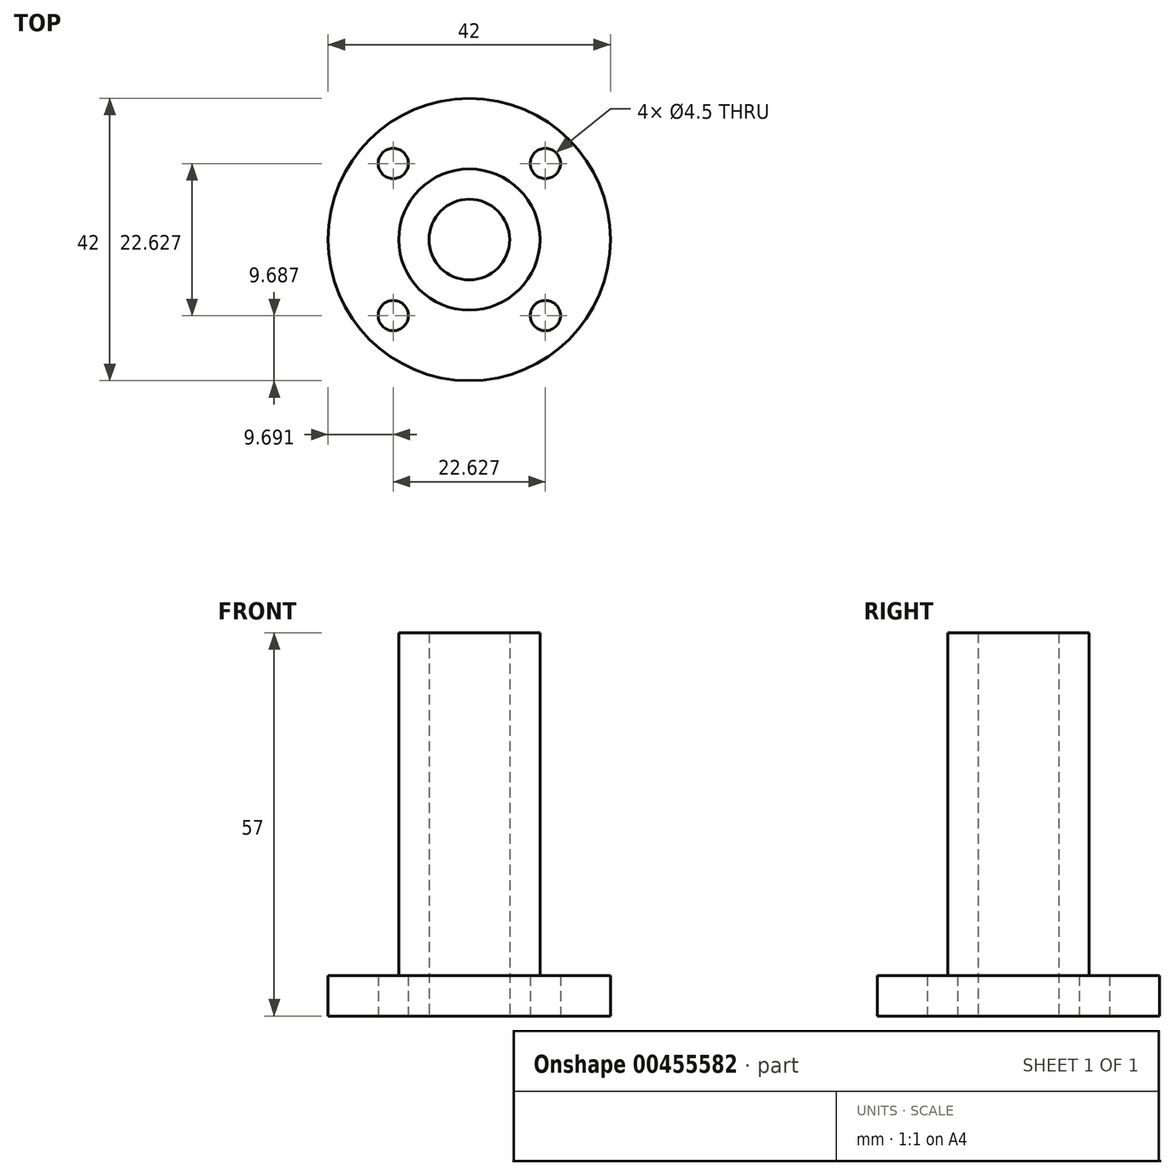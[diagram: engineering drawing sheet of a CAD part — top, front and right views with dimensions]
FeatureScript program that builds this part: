
annotation { "Feature Type Name" : "Feature", "Feature Type Description" : "" }
export const myFeature = defineFeature(function(context is Context, id is Id, definition is map)
    precondition{}
    {
        {
            var Q0;
            Q0=qCreatedBy(makeId("Top.planeOp"),FACE);
            var sketch = newSketch(context, id + "F0", { "sketchPlane" : qUnion([Q0])});
            skCircle(sketch, "E0", {"center": v(-9.89, 3.31) * mm, "radius": 6 * mm});
            skCircle(sketch, "E1", {"center": v(-9.89, 3.31) * mm, "radius": 10.5 * mm});
            skCircle(sketch, "E2", {"center": v(-9.89, 3.31) * mm, "radius": 21 * mm});
            skCircle(sketch, "E3", {"center": v(-9.89, 3.31) * mm, "radius": 16 * mm, "construction": true});
            skCircle(sketch, "E4", {"center": v(-21.2, 14.62) * mm, "radius": 2.25 * mm});
            skCircle(sketch, "E5.1.0", {"center": v(1.43, 14.62) * mm, "radius": 2.25 * mm});
            skCircle(sketch, "E5.2.0", {"center": v(1.43, -8) * mm, "radius": 2.25 * mm});
            skCircle(sketch, "E5.3.0", {"center": v(-21.2, -8) * mm, "radius": 2.25 * mm});
            skLineSegment(sketch, "E5.anchor1", {"start": v(-9.89, 3.31) * mm, "end": v(-21.2, 14.62) * mm, "construction": true});
            skLineSegment(sketch, "E5.anchor2", {"start": v(-9.89, 3.31) * mm, "end": v(-21.2, -8) * mm, "construction": true});
            skSolve(sketch);
        }
        {
            var Q0;
            Q0=makeQuery(id+"F0.imprint","IMPRINT",FACE,{"disambiguationData":[TD([[makeQuery(id+"F0.imprint","IMPRINT",EDGE,{"derivedFrom":sQuery(id+"F0.wireOp",EDGE,"E0")}),-1.0]])]});
            extrude(context, id + "F1", {"entities" : qUnion([Q0]), "depth" : 57 * mm});
        }
        {
            var Q0;
            Q0=makeQuery(id+"F0.imprint","IMPRINT",FACE,{"disambiguationData":[TD([[makeQuery(id+"F0.imprint","IMPRINT",EDGE,{"derivedFrom":sQuery(id+"F0.wireOp",EDGE,"E1")}),-1.0]])]});
            extrude(context, id + "F2", {"entities" : qUnion([Q0]), "operationType" : NewBodyOperationType.ADD, "depth" : 6 * mm});
        }
    });
